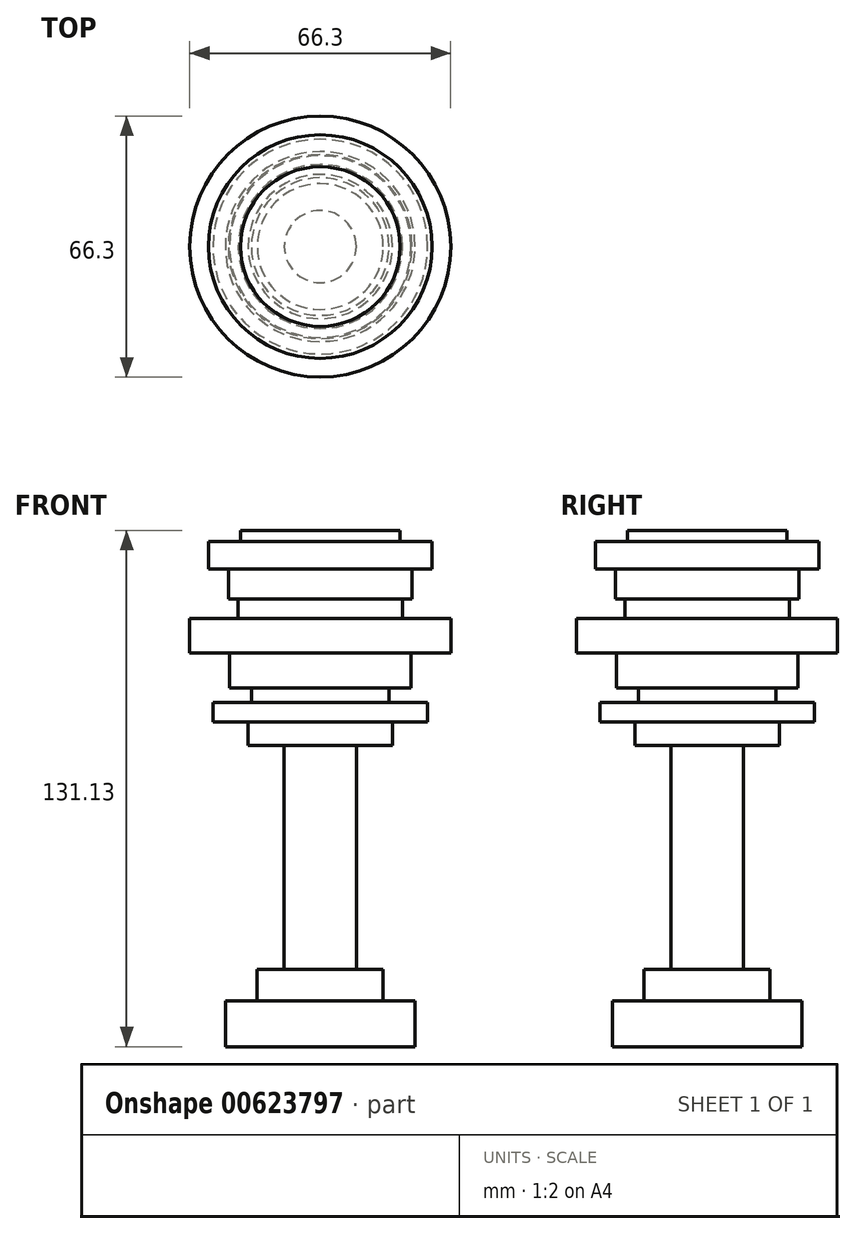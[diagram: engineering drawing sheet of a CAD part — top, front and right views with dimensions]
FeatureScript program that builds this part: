
annotation { "Feature Type Name" : "Feature", "Feature Type Description" : "" }
export const myFeature = defineFeature(function(context is Context, id is Id, definition is map)
    precondition{}
    {
        {
            var Q0;
            Q0=qCreatedBy(makeId("Front.planeOp"),FACE);
            var sketch = newSketch(context, id + "F0", { "sketchPlane" : qUnion([Q0])});
            skLineSegment(sketch, "E0.bottom", {"start": v(0, 36.23) * mm, "end": v(-20.28, 36.23) * mm});
            skLineSegment(sketch, "E0.top", {"start": v(0, 33.43) * mm, "end": v(-20.28, 33.43) * mm});
            skLineSegment(sketch, "E0.left", {"start": v(0, 36.23) * mm, "end": v(0, 33.43) * mm});
            skLineSegment(sketch, "E0.right", {"start": v(-20.28, 36.23) * mm, "end": v(-20.28, 33.43) * mm});
            skLineSegment(sketch, "E1.bottom", {"start": v(0, 33.43) * mm, "end": v(-28.4, 33.43) * mm});
            skLineSegment(sketch, "E1.top", {"start": v(0, 26.44) * mm, "end": v(-28.4, 26.44) * mm});
            skLineSegment(sketch, "E1.left", {"start": v(0, 33.43) * mm, "end": v(0, 26.44) * mm});
            skLineSegment(sketch, "E1.right", {"start": v(-28.4, 33.43) * mm, "end": v(-28.4, 26.44) * mm});
            skLineSegment(sketch, "E2.bottom", {"start": v(0, 26.44) * mm, "end": v(-23.36, 26.44) * mm});
            skLineSegment(sketch, "E2.top", {"start": v(0, 18.88) * mm, "end": v(-23.36, 18.88) * mm});
            skLineSegment(sketch, "E2.left", {"start": v(0, 26.44) * mm, "end": v(0, 18.88) * mm});
            skLineSegment(sketch, "E2.right", {"start": v(-23.36, 26.44) * mm, "end": v(-23.36, 18.88) * mm});
            skLineSegment(sketch, "E3.bottom", {"start": v(0, 18.88) * mm, "end": v(-20.84, 18.88) * mm});
            skLineSegment(sketch, "E3.top", {"start": v(0, 13.85) * mm, "end": v(-20.84, 13.85) * mm});
            skLineSegment(sketch, "E3.left", {"start": v(0, 18.88) * mm, "end": v(0, 13.85) * mm});
            skLineSegment(sketch, "E3.right", {"start": v(-20.84, 18.88) * mm, "end": v(-20.84, 13.85) * mm});
            skLineSegment(sketch, "E4.bottom", {"start": v(0, 13.85) * mm, "end": v(-33.15, 13.85) * mm});
            skLineSegment(sketch, "E4.top", {"start": v(0, 5.18) * mm, "end": v(-33.15, 5.18) * mm});
            skLineSegment(sketch, "E4.left", {"start": v(0, 13.85) * mm, "end": v(0, 5.18) * mm});
            skLineSegment(sketch, "E4.right", {"start": v(-33.15, 13.85) * mm, "end": v(-33.15, 5.18) * mm});
            skLineSegment(sketch, "E5.bottom", {"start": v(0, 5.18) * mm, "end": v(-23.08, 5.18) * mm});
            skLineSegment(sketch, "E5.top", {"start": v(0, -3.78) * mm, "end": v(-23.08, -3.78) * mm});
            skLineSegment(sketch, "E5.left", {"start": v(0, 5.18) * mm, "end": v(0, -3.78) * mm});
            skLineSegment(sketch, "E5.right", {"start": v(-23.08, 5.18) * mm, "end": v(-23.08, -3.78) * mm});
            skLineSegment(sketch, "E6.bottom", {"start": v(0, -3.78) * mm, "end": v(-17.48, -3.78) * mm});
            skLineSegment(sketch, "E6.top", {"start": v(0, -7.41) * mm, "end": v(-17.48, -7.41) * mm});
            skLineSegment(sketch, "E6.left", {"start": v(0, -3.78) * mm, "end": v(0, -7.41) * mm});
            skLineSegment(sketch, "E6.right", {"start": v(-17.48, -3.78) * mm, "end": v(-17.48, -7.41) * mm});
            skLineSegment(sketch, "E7.bottom", {"start": v(0, -7.41) * mm, "end": v(-27.28, -7.41) * mm});
            skLineSegment(sketch, "E7.top", {"start": v(0, -12.45) * mm, "end": v(-27.28, -12.45) * mm});
            skLineSegment(sketch, "E7.left", {"start": v(0, -7.41) * mm, "end": v(0, -12.45) * mm});
            skLineSegment(sketch, "E7.right", {"start": v(-27.28, -7.41) * mm, "end": v(-27.28, -12.45) * mm});
            skLineSegment(sketch, "E8.bottom", {"start": v(0, -12.45) * mm, "end": v(-18.32, -12.45) * mm});
            skLineSegment(sketch, "E8.top", {"start": v(0, -18.32) * mm, "end": v(-18.32, -18.32) * mm});
            skLineSegment(sketch, "E8.left", {"start": v(0, -12.45) * mm, "end": v(0, -18.32) * mm});
            skLineSegment(sketch, "E8.right", {"start": v(-18.32, -12.45) * mm, "end": v(-18.32, -18.32) * mm});
            skPoint(sketch, "E9.oppositeSnap0", {"position": v(-9.16, -18.32) * mm});
            skLineSegment(sketch, "E9.bottom", {"start": v(0, -18.32) * mm, "end": v(-9.16, -18.32) * mm});
            skLineSegment(sketch, "E9.top", {"start": v(0, -75.3) * mm, "end": v(-9.16, -75.3) * mm});
            skLineSegment(sketch, "E9.left", {"start": v(0, -18.32) * mm, "end": v(0, -75.3) * mm});
            skLineSegment(sketch, "E9.right", {"start": v(-9.16, -18.32) * mm, "end": v(-9.16, -75.3) * mm});
            skLineSegment(sketch, "E10.bottom", {"start": v(0, -75.3) * mm, "end": v(-16, -75.3) * mm});
            skLineSegment(sketch, "E10.top", {"start": v(0, -83.3) * mm, "end": v(-16, -83.3) * mm});
            skLineSegment(sketch, "E10.left", {"start": v(0, -75.3) * mm, "end": v(0, -83.3) * mm});
            skLineSegment(sketch, "E10.right", {"start": v(-16, -75.3) * mm, "end": v(-16, -83.3) * mm});
            skLineSegment(sketch, "E11.bottom", {"start": v(0, -83.3) * mm, "end": v(-24.12, -83.3) * mm});
            skLineSegment(sketch, "E11.top", {"start": v(0, -94.9) * mm, "end": v(-24.12, -94.9) * mm});
            skLineSegment(sketch, "E11.left", {"start": v(0, -83.3) * mm, "end": v(0, -94.9) * mm});
            skLineSegment(sketch, "E11.right", {"start": v(-24.12, -83.3) * mm, "end": v(-24.12, -94.9) * mm});
            skSolve(sketch);
        }
        {
            var Q0;
            Q0 = qSketchRegion(id + "F0", true);
            var Q1;
            Q1=sQuery(id+"F0.wireOp",EDGE,"E9.left");
            revolve(context, id + "F1", {"entities" : qUnion([Q0]), "axis" : qUnion([Q1]), "revolveType" : RevolveType.FULL});
        }
    });
